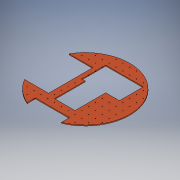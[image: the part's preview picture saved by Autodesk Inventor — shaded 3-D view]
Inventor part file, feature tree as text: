
AUTODESK INVENTOR PART (.ipt)
format: ipt  version: 2018 (Build 220112000, 112)  size: 246,272 bytes
history: native  units: in
note: dims shown in document units (in); Inventor stores cm internally (conversion verified against a paired STEP export)
features: sketch x3, extrude x2, hole x1, pattern_linear x1
ambient origin geometry x8: Origin, YZ Plane, XZ Plane, XY Plane, X Axis, Y Axis, Z Axis, Center Point
bodies: Solid1 (feature_tree)
feature tree (7):
  extrude  "Extrusion1"  Depth=0.125in TaperAngle=0.0deg
  hole  "Hole1"  [1 undecoded]
  pattern_linear  "Rectangular Pattern1"  Spacing1=3.0in  [1 undecoded]
  extrude  "Extrusion2"  Depth=8.0in
  sketch  "Sketch1"  dims[d0=13.0in d1=0.125in d2=0.0in]
  sketch  "Sketch2"  dims[d3=0.085in d4=0.224in d5=0.375in d6=0.25in d7=0.5635in d8=0.349in d9=0.8108in d10=5.1181in d12=1.0in d13=5.1181in d15=1.0in]
  sketch  "Sketch3"  dims[d16=4.5in d17=3.0in d18=8.0in d19=2.0in d20=5.5in d21=3.5in d22=0.5in d23=1.3in d24=5.0in d25=3.0in d26=6.5in d27=5.0in d28=3.5in d30=3.5in d31=0.125in d32=0.0in d34=0.5in d35=180.0deg]
note: 2 required parameter values undecoded (feature->parameter linkage not recoverable at this tier; creation-order binding heuristic only, values carry confidence <= 0.55)
